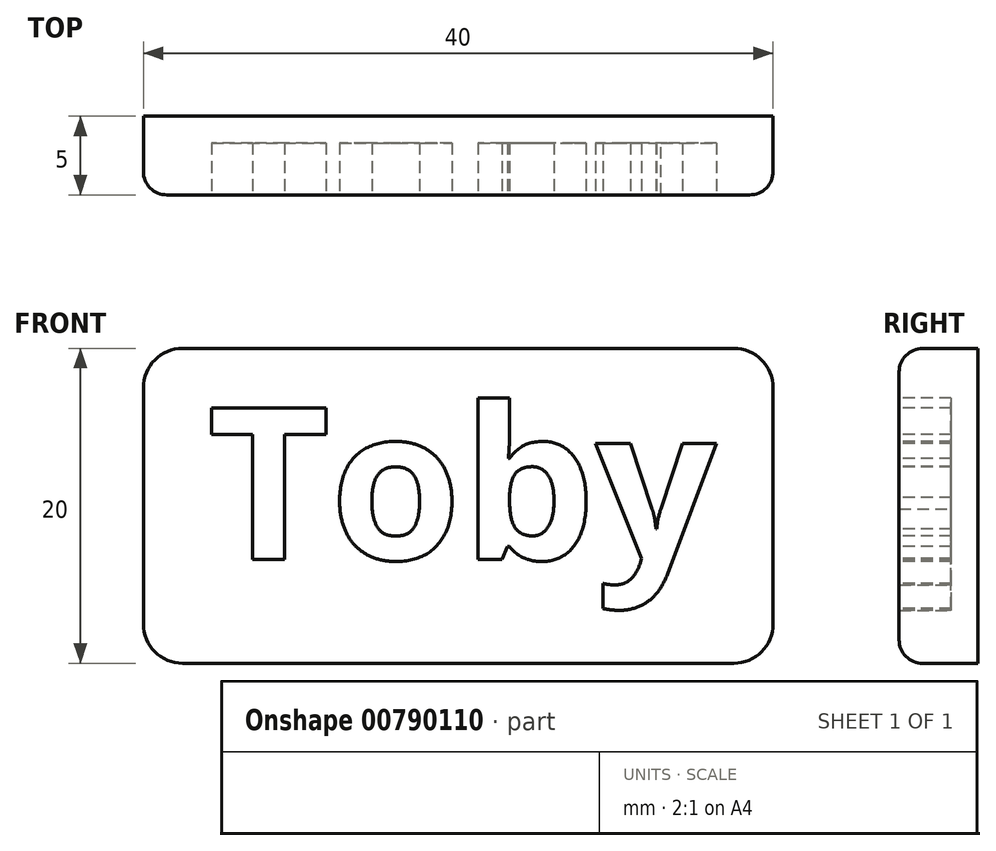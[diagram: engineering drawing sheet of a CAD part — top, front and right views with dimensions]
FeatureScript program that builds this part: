
annotation { "Feature Type Name" : "Feature", "Feature Type Description" : "" }
export const myFeature = defineFeature(function(context is Context, id is Id, definition is map)
    precondition{}
    {
        {
            var Q0;
            Q0=qCreatedBy(makeId("Front.planeOp"),FACE);
            var sketch = newSketch(context, id + "F0", { "sketchPlane" : qUnion([Q0])});
            skLineSegment(sketch, "E0.bottom", {"start": v(-20, 10) * mm, "end": v(20, 10) * mm});
            skLineSegment(sketch, "E0.top", {"start": v(-20, -10) * mm, "end": v(20, -10) * mm});
            skLineSegment(sketch, "E0.left", {"start": v(-20, 10) * mm, "end": v(-20, -10) * mm});
            skLineSegment(sketch, "E0.right", {"start": v(20, 10) * mm, "end": v(20, -10) * mm});
            skPoint(sketch, "E0.middle", {"position": v(0, 0) * mm});
            skSolve(sketch);
        }
        {
            var Q0;
            Q0 = qSketchRegion(id + "F0", true);
            extrude(context, id + "F1", {"entities" : qUnion([Q0]), "depth" : 5 * mm, "offsetDistance" : 25 * mm});
        }
        {
            var Q0;
            Q0=makeQuery(id+"F1.opExtrude","SWEPT_EDGE",EDGE,{"disambiguationData":[OSD([sQuery(id+"F0.wireOp",EDGE,"E0.bottom"),sQuery(id+"F0.wireOp",EDGE,"E0.left")])]});
            var Q1;
            Q1=makeQuery(id+"F1.opExtrude","SWEPT_EDGE",EDGE,{"disambiguationData":[OSD([sQuery(id+"F0.wireOp",EDGE,"E0.top"),sQuery(id+"F0.wireOp",EDGE,"E0.left")])]});
            var Q2;
            Q2=makeQuery(id+"F1.opExtrude","SWEPT_EDGE",EDGE,{"disambiguationData":[OSD([sQuery(id+"F0.wireOp",EDGE,"E0.bottom"),sQuery(id+"F0.wireOp",EDGE,"E0.right")])]});
            var Q3;
            Q3=makeQuery(id+"F1.opExtrude","SWEPT_EDGE",EDGE,{"disambiguationData":[OSD([sQuery(id+"F0.wireOp",EDGE,"E0.top"),sQuery(id+"F0.wireOp",EDGE,"E0.right")])]});
            fillet(context, id + "F2", {"entities" : qUnion([Q0, Q1, Q2, Q3]), "radius" : 2.5 * mm, "tangentPropagation" : true, "allowEdgeOverflow" : false});
        }
        {
            var Q0;
            Q0=makeQuery(id+"F1.opExtrude","CAP_EDGE",EDGE,{"disambiguationData":[OSD([sQuery(id+"F0.wireOp",EDGE,"E0.bottom")])],"isStart":false});
            fillet(context, id + "F3", {"entities" : qUnion([Q0]), "radius" : 1.5 * mm, "tangentPropagation" : true, "allowEdgeOverflow" : false});
        }
        {
            var Q0;
            Q0=makeQuery(id+"F1.opExtrude","CAP_FACE",FACE,{"disambiguationData":[OSD([sQuery(id+"F0.wireOp",EDGE,"E0.bottom"),sQuery(id+"F0.wireOp",EDGE,"E0.top"),sQuery(id+"F0.wireOp",EDGE,"E0.left"),sQuery(id+"F0.wireOp",EDGE,"E0.right")])],"isStart":false});
            var sketch = newSketch(context, id + "F4", { "sketchPlane" : qUnion([Q0])});
            skText(sketch, "E1", { "text": "Toby\n", "fontName": "OpenSans-Bold.ttf"});
            const initialGuessF4  = {"E1": [-0.01594, -0.0034, 1, 0, 0.0097]};
            skSetInitialGuess(sketch, initialGuessF4);
            skSolve(sketch);
        }
        {
            var Q0;
            Q0 = qSketchRegion(id + "F4", true);
            extrude(context, id + "F5", {"entities" : qUnion([Q0]), "operationType" : NewBodyOperationType.REMOVE, "oppositeDirection" : true, "depth" : 3.3 * mm, "offsetDistance" : 25 * mm});
        }
    });
